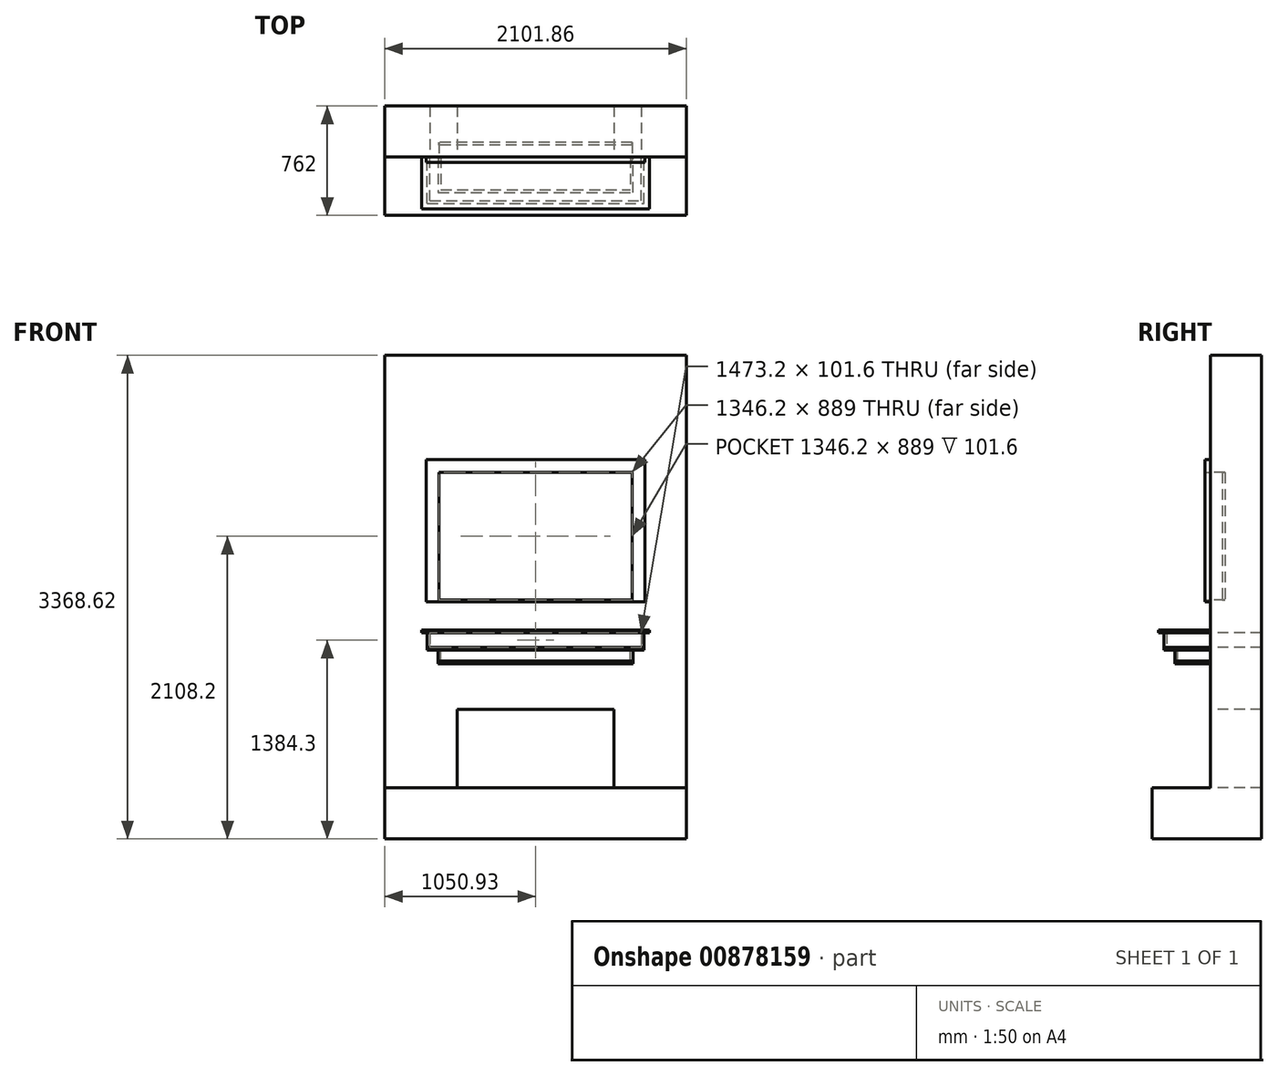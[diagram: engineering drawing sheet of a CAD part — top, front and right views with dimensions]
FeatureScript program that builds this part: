
annotation { "Feature Type Name" : "Feature", "Feature Type Description" : "" }
export const myFeature = defineFeature(function(context is Context, id is Id, definition is map)
    precondition{}
    {
        {
            var Q0;
            Q0=qCreatedBy(makeId("Front.planeOp"),FACE);
            var sketch = newSketch(context, id + "F0", { "sketchPlane" : qUnion([Q0])});
            skLineSegment(sketch, "E0.bottom", {"start": v(-736.6, 0) * mm, "end": v(736.6, 0) * mm});
            skLineSegment(sketch, "E0.top", {"start": v(-736.6, -101.6) * mm, "end": v(736.6, -101.6) * mm});
            skLineSegment(sketch, "E0.left", {"start": v(-736.6, 0) * mm, "end": v(-736.6, -101.6) * mm});
            skLineSegment(sketch, "E0.right", {"start": v(736.6, 0) * mm, "end": v(736.6, -101.6) * mm});
            skSolve(sketch);
        }
        {
            var Q0;
            Q0=makeQuery(id+"F0.imprint","IMPRINT",FACE,{"disambiguationData":[TD([[makeQuery(id+"F0.imprint","IMPRINT",EDGE,{"derivedFrom":sQuery(id+"F0.wireOp",EDGE,"E0.bottom")}),-1.0]])]});
            extrude(context, id + "F1", {"entities" : qUnion([Q0]), "depth" : 304.8 * mm, "offsetDistance" : 25.4 * mm});
        }
        {
            var Q0;
            Q0=makeQuery(id+"F1.opExtrude","SWEPT_FACE",FACE,{"disambiguationData":[OSD([sQuery(id+"F0.wireOp",EDGE,"E0.top")])]});
            var sketch = newSketch(context, id + "F2", { "sketchPlane" : qUnion([Q0])});
            skLineSegment(sketch, "E1.bottom", {"start": v(-755.65, 323.85) * mm, "end": v(755.65, 323.85) * mm});
            skLineSegment(sketch, "E1.top", {"start": v(-755.65, 304.8) * mm, "end": v(755.65, 304.8) * mm});
            skLineSegment(sketch, "E1.left", {"start": v(-755.65, 323.85) * mm, "end": v(-755.65, 304.8) * mm});
            skLineSegment(sketch, "E1.right", {"start": v(755.65, 323.85) * mm, "end": v(755.65, 304.8) * mm});
            skLineSegment(sketch, "E2.bottom", {"start": v(-755.65, 304.8) * mm, "end": v(-736.6, 304.8) * mm});
            skLineSegment(sketch, "E2.top", {"start": v(-755.65, 0) * mm, "end": v(-736.6, 0) * mm});
            skLineSegment(sketch, "E2.left", {"start": v(-755.65, 304.8) * mm, "end": v(-755.65, 0) * mm});
            skLineSegment(sketch, "E2.right", {"start": v(-736.6, 304.8) * mm, "end": v(-736.6, 0) * mm});
            skLineSegment(sketch, "E3.bottom", {"start": v(755.65, 304.8) * mm, "end": v(736.6, 304.8) * mm});
            skLineSegment(sketch, "E3.top", {"start": v(755.65, 0) * mm, "end": v(736.6, 0) * mm});
            skLineSegment(sketch, "E3.left", {"start": v(755.65, 304.8) * mm, "end": v(755.65, 0) * mm});
            skLineSegment(sketch, "E3.right", {"start": v(736.6, 304.8) * mm, "end": v(736.6, 0) * mm});
            skSolve(sketch);
        }
        {
            var Q0;
            Q0=makeQuery(id+"F2.imprint","IMPRINT",FACE,{"disambiguationData":[TD([[makeQuery(id+"F2.imprint","IMPRINT",EDGE,{"derivedFrom":sQuery(id+"F2.wireOp",EDGE,"E1.bottom")}),-1.0]])]});
            var Q1;
            Q1=makeQuery(id+"F2.imprint","IMPRINT",FACE,{"disambiguationData":[TD([[makeQuery(id+"F2.imprint","IMPRINT",EDGE,{"derivedFrom":sQuery(id+"F2.wireOp",EDGE,"E2.top")}),1.0]])]});
            var Q2;
            Q2=makeQuery(id+"F2.imprint","IMPRINT",FACE,{"disambiguationData":[TD([[makeQuery(id+"F2.imprint","IMPRINT",EDGE,{"derivedFrom":sQuery(id+"F2.wireOp",EDGE,"E3.top")}),-1.0]])]});
            var Q3;
            Q3=makeQuery(id+"F1.opExtrude","SWEPT_FACE",FACE,{"disambiguationData":[OSD([sQuery(id+"F0.wireOp",EDGE,"E0.bottom")])]});
            extrude(context, id + "F3", {"entities" : qUnion([Q0, Q1, Q2]), "endBound" : BoundingType.UP_TO_SURFACE, "oppositeDirection" : true, "depth" : 256.2 * mm, "endBoundEntityFace" : qUnion([Q3]), "offsetDistance" : 25.4 * mm});
        }
        {
            var Q0;
            Q0=makeQuery(id+"F1.opExtrude","SWEPT_FACE",FACE,{"disambiguationData":[OSD([sQuery(id+"F0.wireOp",EDGE,"E0.top")])]});
            var sketch = newSketch(context, id + "F4", { "sketchPlane" : qUnion([Q0])});
            skLineSegment(sketch, "E4.bottom", {"start": v(-755.65, 323.85) * mm, "end": v(755.65, 323.85) * mm});
            skLineSegment(sketch, "E4.top", {"start": v(-755.65, 0) * mm, "end": v(755.65, 0) * mm});
            skLineSegment(sketch, "E4.left", {"start": v(-755.65, 323.85) * mm, "end": v(-755.65, 0) * mm});
            skLineSegment(sketch, "E4.right", {"start": v(755.65, 323.85) * mm, "end": v(755.65, 0) * mm});
            skSolve(sketch);
        }
        {
            var Q0;
            Q0=makeQuery(id+"F4.imprint","IMPRINT",FACE,{"disambiguationData":[TD([[makeQuery(id+"F4.imprint","IMPRINT",EDGE,{"derivedFrom":sQuery(id+"F4.wireOp",EDGE,"E4.bottom")}),-1.0]])]});
            var Q1;
            {var subQ1=sQuery(id+"F0.wireOp",EDGE,"E0.top");Q1=makeQuery(id+"F4.imprint","IMPRINT",FACE,{"disambiguationData":[TD([[makeQuery(id+"F4.imprint","IMPRINT",EDGE,{"derivedFrom":makeQuery(id+"F1.opExtrude","CAP_EDGE",EDGE,{"disambiguationData":[OSD([subQ1])],"isStart":false})}),-1.0]])]});}
            extrude(context, id + "F5", {"entities" : qUnion([Q0, Q1]), "depth" : 19.05 * mm, "offsetDistance" : 25.4 * mm});
        }
        {
            var Q0;
            Q0=makeQuery(id+"F1.opExtrude","SWEPT_FACE",FACE,{"disambiguationData":[OSD([sQuery(id+"F0.wireOp",EDGE,"E0.bottom")])]});
            var sketch = newSketch(context, id + "F6", { "sketchPlane" : qUnion([Q0])});
            skLineSegment(sketch, "E5.bottom", {"start": v(-755.65, 0) * mm, "end": v(755.65, 0) * mm});
            skLineSegment(sketch, "E6", {"start": v(755.65, 0) * mm, "end": v(793.75, 0) * mm});
            skLineSegment(sketch, "E7", {"start": v(793.75, 0) * mm, "end": v(793.75, -361.95) * mm});
            skLineSegment(sketch, "E8", {"start": v(793.75, -361.95) * mm, "end": v(-793.75, -361.95) * mm});
            skLineSegment(sketch, "E9", {"start": v(-793.75, -361.95) * mm, "end": v(-793.75, 0) * mm});
            skLineSegment(sketch, "E10", {"start": v(-793.75, 0) * mm, "end": v(-755.65, 0) * mm});
            skLineSegment(sketch, "E11", {"start": v(755.65, -361.95) * mm, "end": v(755.65, -323.85) * mm, "construction": true});
            skSolve(sketch);
        }
        {
            var Q0;
            {var subQ1=sQuery(id+"F0.wireOp",EDGE,"E0.bottom");Q0=makeQuery(id+"F6.imprint","IMPRINT",FACE,{"disambiguationData":[TD([[makeQuery(id+"F6.imprint","IMPRINT",EDGE,{"derivedFrom":makeQuery(id+"F1.opExtrude","CAP_EDGE",EDGE,{"disambiguationData":[OSD([subQ1])],"isStart":false})}),1.0]])]});}
            var Q1;
            {var subQ0=sQuery(id+"F6.wireOp",EDGE,"E6");Q1=makeQuery(id+"F6.imprint","IMPRINT",FACE,{"disambiguationData":[TD([[makeQuery(id+"F6.imprint","IMPRINT",EDGE,{"derivedFrom":subQ0}),-1.0]])]});}
            extrude(context, id + "F7", {"entities" : qUnion([Q0, Q1]), "depth" : 19.05 * mm, "offsetDistance" : 25.4 * mm});
        }
        {
            var Q0;
            Q0=makeQuery(id+"F5.opExtrude","CAP_FACE",FACE,{"disambiguationData":[OSD([sQuery(id+"F4.wireOp",EDGE,"E4.bottom"),sQuery(id+"F4.wireOp",EDGE,"E4.top"),sQuery(id+"F4.wireOp",EDGE,"E4.left"),sQuery(id+"F4.wireOp",EDGE,"E4.right")])],"isStart":false});
            var sketch = newSketch(context, id + "F8", { "sketchPlane" : qUnion([Q0])});
            skLineSegment(sketch, "E12.bottom", {"start": v(-679.45, 0) * mm, "end": v(-660.4, 0) * mm});
            skLineSegment(sketch, "E12.top", {"start": v(-679.45, 228.6) * mm, "end": v(-660.4, 228.6) * mm});
            skLineSegment(sketch, "E12.left", {"start": v(-679.45, 0) * mm, "end": v(-679.45, 228.6) * mm});
            skLineSegment(sketch, "E12.right", {"start": v(-660.4, 0) * mm, "end": v(-660.4, 228.6) * mm});
            skLineSegment(sketch, "E13.bottom", {"start": v(679.45, 0) * mm, "end": v(660.4, 0) * mm});
            skLineSegment(sketch, "E13.top", {"start": v(679.45, 228.6) * mm, "end": v(660.4, 228.6) * mm});
            skLineSegment(sketch, "E13.left", {"start": v(679.45, 0) * mm, "end": v(679.45, 228.6) * mm});
            skLineSegment(sketch, "E13.right", {"start": v(660.4, 0) * mm, "end": v(660.4, 228.6) * mm});
            skLineSegment(sketch, "E14.bottom", {"start": v(-679.45, 247.65) * mm, "end": v(679.45, 247.65) * mm});
            skLineSegment(sketch, "E14.top", {"start": v(-679.45, 228.6) * mm, "end": v(679.45, 228.6) * mm});
            skLineSegment(sketch, "E14.left", {"start": v(-679.45, 247.65) * mm, "end": v(-679.45, 228.6) * mm});
            skLineSegment(sketch, "E14.right", {"start": v(679.45, 247.65) * mm, "end": v(679.45, 228.6) * mm});
            skLineSegment(sketch, "E15", {"start": v(-679.45, 247.65) * mm, "end": v(-755.65, 247.65) * mm, "construction": true});
            skLineSegment(sketch, "E16", {"start": v(679.45, 247.65) * mm, "end": v(755.65, 247.65) * mm, "construction": true});
            skLineSegment(sketch, "E17", {"start": v(-679.45, 247.65) * mm, "end": v(-679.45, 323.85) * mm, "construction": true});
            skSolve(sketch);
        }
        {
            var Q0;
            Q0=makeQuery(id+"F8.imprint","IMPRINT",FACE,{"disambiguationData":[TD([[makeQuery(id+"F8.imprint","IMPRINT",EDGE,{"derivedFrom":sQuery(id+"F8.wireOp",EDGE,"E12.bottom")}),1.0]])]});
            var Q1;
            Q1=makeQuery(id+"F8.imprint","IMPRINT",FACE,{"disambiguationData":[TD([[makeQuery(id+"F8.imprint","IMPRINT",EDGE,{"derivedFrom":sQuery(id+"F8.wireOp",EDGE,"E12.top")}),1.0]])]});
            var Q2;
            Q2=makeQuery(id+"F8.imprint","IMPRINT",FACE,{"disambiguationData":[TD([[makeQuery(id+"F8.imprint","IMPRINT",EDGE,{"derivedFrom":sQuery(id+"F8.wireOp",EDGE,"E13.bottom")}),1.0]])]});
            extrude(context, id + "F9", {"entities" : qUnion([Q0, Q1, Q2]), "depth" : 76.2 * mm, "offsetDistance" : 25.4 * mm});
        }
        {
            var Q0;
            Q0=makeQuery(id+"F9.opExtrude","CAP_FACE",FACE,{"disambiguationData":[OSD([sQuery(id+"F8.wireOp",EDGE,"E12.bottom"),sQuery(id+"F8.wireOp",EDGE,"E12.left"),sQuery(id+"F8.wireOp",EDGE,"E12.right"),sQuery(id+"F8.wireOp",EDGE,"E13.bottom"),sQuery(id+"F8.wireOp",EDGE,"E13.left"),sQuery(id+"F8.wireOp",EDGE,"E13.right"),sQuery(id+"F8.wireOp",EDGE,"E14.bottom"),sQuery(id+"F8.wireOp",EDGE,"E14.top"),sQuery(id+"F8.wireOp",EDGE,"E14.left"),sQuery(id+"F8.wireOp",EDGE,"E14.right")])],"isStart":false});
            var sketch = newSketch(context, id + "F10", { "sketchPlane" : qUnion([Q0])});
            skLineSegment(sketch, "E18.bottom", {"start": v(679.45, 247.65) * mm, "end": v(-679.45, 247.65) * mm});
            skLineSegment(sketch, "E18.top", {"start": v(679.45, 0) * mm, "end": v(-679.45, 0) * mm});
            skLineSegment(sketch, "E18.left", {"start": v(679.45, 247.65) * mm, "end": v(679.45, 0) * mm});
            skLineSegment(sketch, "E18.right", {"start": v(-679.45, 247.65) * mm, "end": v(-679.45, 0) * mm});
            skSolve(sketch);
        }
        {
            var Q0;
            Q0=makeQuery(id+"F10.imprint","IMPRINT",FACE,{"disambiguationData":[TD([[makeQuery(id+"F10.imprint","IMPRINT",EDGE,{"derivedFrom":sQuery(id+"F10.wireOp",EDGE,"E18.bottom")}),-1.0]])]});
            var Q1;
            {var subQ1=makeQuery(id+"F9.opExtrude","CAP_EDGE",EDGE,{"disambiguationData":[OSD([sQuery(id+"F8.wireOp",EDGE,"E12.right")])],"isStart":false});Q1=makeQuery(id+"F10.imprint","IMPRINT",FACE,{"disambiguationData":[TD([[makeQuery(id+"F10.imprint","IMPRINT",EDGE,{"derivedFrom":subQ1}),-1.0]])]});}
            extrude(context, id + "F11", {"entities" : qUnion([Q0, Q1]), "depth" : 19.05 * mm, "offsetDistance" : 25.4 * mm});
        }
        {
            var Q0;
            Q0=makeQuery(id+"F1.opExtrude","CAP_FACE",FACE,{"disambiguationData":[OSD([sQuery(id+"F0.wireOp",EDGE,"E0.bottom"),sQuery(id+"F0.wireOp",EDGE,"E0.top"),sQuery(id+"F0.wireOp",EDGE,"E0.left"),sQuery(id+"F0.wireOp",EDGE,"E0.right")])],"isStart":true});
            var sketch = newSketch(context, id + "F12", { "sketchPlane" : qUnion([Q0])});
            skLineSegment(sketch, "E19.top", {"start": v(-1050.93, -1079.5) * mm, "end": v(1050.93, -1079.5) * mm});
            skLineSegment(sketch, "E19.left", {"start": v(-1050.93, 1117.6) * mm, "end": v(-1050.93, -1079.5) * mm});
            skLineSegment(sketch, "E19.right", {"start": v(1050.93, 1117.6) * mm, "end": v(1050.93, -1079.5) * mm});
            skLineSegment(sketch, "E20", {"start": v(0, 1117.6) * mm, "end": v(0, -1079.5) * mm, "construction": true});
            skPoint(sketch, "E21", {"position": v(0, 19.05) * mm});
            skLineSegment(sketch, "E22.bottom", {"start": v(-673.1, 1117.6) * mm, "end": v(673.1, 1117.6) * mm});
            skLineSegment(sketch, "E22.top", {"start": v(-673.1, 228.6) * mm, "end": v(673.1, 228.6) * mm});
            skLineSegment(sketch, "E22.left", {"start": v(-673.1, 1117.6) * mm, "end": v(-673.1, 228.6) * mm});
            skLineSegment(sketch, "E22.right", {"start": v(673.1, 1117.6) * mm, "end": v(673.1, 228.6) * mm});
            skPoint(sketch, "E23", {"position": v(0, 1117.6) * mm});
            skLineSegment(sketch, "E24.bottom", {"start": v(-546.1, -1079.5) * mm, "end": v(546.1, -1079.5) * mm});
            skLineSegment(sketch, "E24.top", {"start": v(-546.1, -533.4) * mm, "end": v(546.1, -533.4) * mm});
            skLineSegment(sketch, "E24.left", {"start": v(-546.1, -1079.5) * mm, "end": v(-546.1, -533.4) * mm});
            skLineSegment(sketch, "E24.right", {"start": v(546.1, -1079.5) * mm, "end": v(546.1, -533.4) * mm});
            skPoint(sketch, "E25", {"position": v(0, -533.4) * mm});
            skLineSegment(sketch, "E26.top", {"start": v(1050.93, 1933.52) * mm, "end": v(-1050.92, 1933.52) * mm});
            skLineSegment(sketch, "E26.left", {"start": v(1050.93, 1117.6) * mm, "end": v(1050.93, 1933.52) * mm});
            skLineSegment(sketch, "E26.right", {"start": v(-1050.92, 1117.6) * mm, "end": v(-1050.92, 1933.52) * mm});
            skLineSegment(sketch, "E27", {"start": v(0, 1117.6) * mm, "end": v(0, 1933.52) * mm, "construction": true});
            skSolve(sketch);
        }
        {
            var Q0;
            {var subQ4=sQuery(id+"F12.wireOp",EDGE,"E19.left");Q0=makeQuery(id+"F12.imprint","IMPRINT",FACE,{"disambiguationData":[TD([[makeQuery(id+"F12.imprint","IMPRINT",EDGE,{"derivedFrom":subQ4}),1.0]])]});}
            var Q1;
            Q1=makeQuery(id+"F12.imprint","IMPRINT",FACE,{"disambiguationData":[TD([[makeQuery(id+"F12.imprint","IMPRINT",EDGE,{"derivedFrom":sQuery(id+"F12.wireOp",EDGE,"E22.bottom")}),-1.0]])]});
            extrude(context, id + "F13", {"entities" : qUnion([Q0, Q1]), "depth" : 355.6 * mm, "offsetDistance" : 25.4 * mm});
        }
        {
            var Q0;
            Q0=makeQuery(id+"F12.imprint","IMPRINT",FACE,{"disambiguationData":[TD([[makeQuery(id+"F12.imprint","IMPRINT",EDGE,{"derivedFrom":sQuery(id+"F12.wireOp",EDGE,"E22.bottom")}),-1.0]])]});
            extrude(context, id + "F14", {"entities" : qUnion([Q0]), "operationType" : NewBodyOperationType.REMOVE, "depth" : 101.6 * mm, "offsetDistance" : 25.4 * mm});
        }
        {
            var Q0;
            {var subQ0=sQuery(id+"F12.wireOp",EDGE,"E19.top");Q0=makeQuery(id+"F13.opExtrude","SWEPT_FACE",FACE,{"disambiguationData":[OSD([subQ0]),TDD([makeQuery(id+"F12.imprint","IMPRINT",EDGE,{"disambiguationData":[TD([[makeQuery(id+"F12.imprint","INTERSECT",VERTEX,{"derivedFrom":[subQ0,sQuery(id+"F12.wireOp",EDGE,"E19.right")]}),1.0]])],"derivedFrom":subQ0})])]});}
            var sketch = newSketch(context, id + "F15", { "sketchPlane" : qUnion([Q0])});
            skLineSegment(sketch, "E28.bottom", {"start": v(-1050.93, -355.6) * mm, "end": v(1050.92, -355.6) * mm});
            skLineSegment(sketch, "E28.top", {"start": v(-1050.93, 406.4) * mm, "end": v(1050.92, 406.4) * mm});
            skLineSegment(sketch, "E28.left", {"start": v(-1050.93, -355.6) * mm, "end": v(-1050.93, 406.4) * mm});
            skLineSegment(sketch, "E28.right", {"start": v(1050.93, -355.6) * mm, "end": v(1050.93, 406.4) * mm});
            skSolve(sketch);
        }
        {
            var Q0;
            {var subQ5=sQuery(id+"F15.wireOp",EDGE,"E28.top");Q0=makeQuery(id+"F15.imprint","IMPRINT",FACE,{"disambiguationData":[TD([[makeQuery(id+"F15.imprint","IMPRINT",EDGE,{"derivedFrom":subQ5}),-1.0]])]});}
            var Q1;
            {var subQ3=sQuery(id+"F12.wireOp",EDGE,"E24.right");var subQ4=sQuery(id+"F12.wireOp",EDGE,"E19.top");var subQ5=makeQuery(id+"F13.opExtrude","SWEPT_EDGE",EDGE,{"disambiguationData":[OSD([subQ4,subQ3])]});Q1=makeQuery(id+"F15.imprint","IMPRINT",FACE,{"disambiguationData":[TD([[makeQuery(id+"F15.imprint","IMPRINT",EDGE,{"derivedFrom":subQ5}),1.0]])]});}
            extrude(context, id + "F16", {"entities" : qUnion([Q0, Q1]), "operationType" : NewBodyOperationType.ADD, "depth" : 355.6 * mm, "offsetDistance" : 25.4 * mm});
        }
        {
            var Q0;
            Q0=makeQuery(id+"F13.opExtrude","CAP_FACE",FACE,{"disambiguationData":[OSD([sQuery(id+"F0.wireOp",EDGE,"E0.bottom"),sQuery(id+"F0.wireOp",EDGE,"E0.top"),sQuery(id+"F0.wireOp",EDGE,"E0.left"),sQuery(id+"F0.wireOp",EDGE,"E0.right"),sQuery(id+"F12.wireOp",EDGE,"E19.top"),sQuery(id+"F12.wireOp",EDGE,"E19.left"),sQuery(id+"F12.wireOp",EDGE,"E19.right"),sQuery(id+"F12.wireOp",EDGE,"E24.top"),sQuery(id+"F12.wireOp",EDGE,"E24.left"),sQuery(id+"F12.wireOp",EDGE,"E24.right"),sQuery(id+"F12.wireOp",EDGE,"E26.top"),sQuery(id+"F12.wireOp",EDGE,"E26.left"),sQuery(id+"F12.wireOp",EDGE,"E26.right")])],"isStart":true});
            var sketch = newSketch(context, id + "F17", { "sketchPlane" : qUnion([Q0])});
            skLineSegment(sketch, "E29.bottom", {"start": v(-552.45, -215.9) * mm, "end": v(-400.05, -215.9) * mm});
            skLineSegment(sketch, "E29.top", {"start": v(-552.45, -444.5) * mm, "end": v(-400.05, -444.5) * mm, "construction": true});
            skLineSegment(sketch, "E29.left", {"start": v(-552.45, -215.9) * mm, "end": v(-552.45, -444.5) * mm});
            skLineSegment(sketch, "E29.right", {"start": v(-400.05, -215.9) * mm, "end": v(-400.05, -444.5) * mm});
            skLineSegment(sketch, "E30.bottom", {"start": v(400.05, -215.9) * mm, "end": v(552.45, -215.9) * mm});
            skLineSegment(sketch, "E30.top", {"start": v(400.05, -444.5) * mm, "end": v(552.45, -444.5) * mm, "construction": true});
            skLineSegment(sketch, "E30.left", {"start": v(400.05, -215.9) * mm, "end": v(400.05, -444.5) * mm});
            skLineSegment(sketch, "E30.right", {"start": v(552.45, -215.9) * mm, "end": v(552.45, -444.5) * mm});
            skLineSegment(sketch, "E31", {"start": v(-552.45, -215.9) * mm, "end": v(-679.45, -215.9) * mm, "construction": true});
            skLineSegment(sketch, "E32", {"start": v(552.45, -215.9) * mm, "end": v(679.45, -215.9) * mm, "construction": true});
            skLineSegment(sketch, "E33", {"start": v(-476.25, -444.5) * mm, "end": v(-476.25, -215.9) * mm});
            skLineSegment(sketch, "E34", {"start": v(476.25, -444.5) * mm, "end": v(476.25, -215.9) * mm});
            skLineSegment(sketch, "E35", {"start": v(-552.45, -215.9) * mm, "end": v(-514.35, -444.5) * mm});
            skLineSegment(sketch, "E36", {"start": v(-438.15, -444.5) * mm, "end": v(-400.05, -215.9) * mm});
            skLineSegment(sketch, "E37", {"start": v(400.05, -215.9) * mm, "end": v(438.15, -444.5) * mm});
            skLineSegment(sketch, "E38", {"start": v(514.35, -444.5) * mm, "end": v(552.45, -215.9) * mm});
            skLineSegment(sketch, "E39", {"start": v(-514.35, -444.5) * mm, "end": v(-438.15, -444.5) * mm});
            skLineSegment(sketch, "E40", {"start": v(438.15, -444.5) * mm, "end": v(514.35, -444.5) * mm});
            skSolve(sketch);
        }
        {
            var Q0;
            {var subQ2=sQuery(id+"F17.wireOp",EDGE,"E34");Q0=makeQuery(id+"F17.imprint","IMPRINT",FACE,{"disambiguationData":[TD([[makeQuery(id+"F17.imprint","IMPRINT",EDGE,{"derivedFrom":subQ2}),1.0]])]});}
            var Q1;
            {var subQ2=sQuery(id+"F17.wireOp",EDGE,"E33");Q1=makeQuery(id+"F17.imprint","IMPRINT",FACE,{"disambiguationData":[TD([[makeQuery(id+"F17.imprint","IMPRINT",EDGE,{"derivedFrom":subQ2}),-1.0]])]});}
            var Q2;
            {var subQ2=sQuery(id+"F17.wireOp",EDGE,"E34");Q2=makeQuery(id+"F17.imprint","IMPRINT",FACE,{"disambiguationData":[TD([[makeQuery(id+"F17.imprint","IMPRINT",EDGE,{"derivedFrom":subQ2}),-1.0]])]});}
            var Q3;
            {var subQ2=sQuery(id+"F17.wireOp",EDGE,"E33");Q3=makeQuery(id+"F17.imprint","IMPRINT",FACE,{"disambiguationData":[TD([[makeQuery(id+"F17.imprint","IMPRINT",EDGE,{"derivedFrom":subQ2}),1.0]])]});}
            extrude(context, id + "F18", {"entities" : qUnion([Q0, Q1, Q2, Q3]), "depth" : 127 * mm, "offsetDistance" : 25.4 * mm});
        }
        {
            var Q0;
            Q0=makeQuery(id+"F9.opExtrude","SWEPT_FACE",FACE,{"disambiguationData":[OSD([sQuery(id+"F8.wireOp",EDGE,"E12.left"),sQuery(id+"F8.wireOp",EDGE,"E14.left")])]});
            var sketch = newSketch(context, id + "F19", { "sketchPlane" : qUnion([Q0])});
            skLineSegment(sketch, "E41", {"start": v(127, -215.9) * mm, "end": v(50.8, -444.5) * mm});
            skLineSegment(sketch, "E42", {"start": v(50.8, -444.5) * mm, "end": v(127, -444.5) * mm});
            skLineSegment(sketch, "E43", {"start": v(127, -444.5) * mm, "end": v(127, -215.9) * mm});
            skSolve(sketch);
        }
        {
            var Q0;
            Q0=makeQuery(id+"F19.imprint","IMPRINT",FACE,{"disambiguationData":[TD([[makeQuery(id+"F19.imprint","IMPRINT",EDGE,{"derivedFrom":sQuery(id+"F19.wireOp",EDGE,"E41")}),1.0]])]});
            extrude(context, id + "F20", {"entities" : qUnion([Q0]), "operationType" : NewBodyOperationType.REMOVE, "oppositeDirection" : true, "depth" : 1468.66 * mm, "offsetDistance" : 25.4 * mm});
        }
        {
            var Q0;
            Q0=makeQuery(id+"F13.opExtrude","CAP_FACE",FACE,{"disambiguationData":[OSD([sQuery(id+"F0.wireOp",EDGE,"E0.bottom"),sQuery(id+"F0.wireOp",EDGE,"E0.top"),sQuery(id+"F0.wireOp",EDGE,"E0.left"),sQuery(id+"F0.wireOp",EDGE,"E0.right"),sQuery(id+"F12.wireOp",EDGE,"E19.top"),sQuery(id+"F12.wireOp",EDGE,"E19.left"),sQuery(id+"F12.wireOp",EDGE,"E19.right"),sQuery(id+"F12.wireOp",EDGE,"E24.top"),sQuery(id+"F12.wireOp",EDGE,"E24.left"),sQuery(id+"F12.wireOp",EDGE,"E24.right"),sQuery(id+"F12.wireOp",EDGE,"E26.top"),sQuery(id+"F12.wireOp",EDGE,"E26.left"),sQuery(id+"F12.wireOp",EDGE,"E26.right")])],"isStart":true});
            var sketch = newSketch(context, id + "F21", { "sketchPlane" : qUnion([Q0])});
            skLineSegment(sketch, "E44.bottom", {"start": v(-762, 1206.5) * mm, "end": v(762, 1206.5) * mm});
            skLineSegment(sketch, "E44.top", {"start": v(-673.1, 304.8) * mm, "end": v(673.1, 304.8) * mm});
            skLineSegment(sketch, "E44.right", {"start": v(762, 1206.5) * mm, "end": v(762, 1117.6) * mm});
            skLineSegment(sketch, "E45.bottom", {"start": v(-673.1, 1117.6) * mm, "end": v(673.1, 1117.6) * mm});
            skLineSegment(sketch, "E45.top", {"start": v(-673.1, 228.6) * mm, "end": v(673.1, 228.6) * mm});
            skLineSegment(sketch, "E45.left", {"start": v(-673.1, 1117.6) * mm, "end": v(-673.1, 228.6) * mm});
            skLineSegment(sketch, "E45.right", {"start": v(673.1, 1117.6) * mm, "end": v(673.1, 228.6) * mm});
            skLineSegment(sketch, "E46", {"start": v(673.1, 1117.6) * mm, "end": v(762, 1117.6) * mm, "construction": true});
            skLineSegment(sketch, "E47", {"start": v(-673.1, 1117.6) * mm, "end": v(-762, 1117.6) * mm, "construction": true});
            skLineSegment(sketch, "E48", {"start": v(-673.1, 1117.6) * mm, "end": v(-673.1, 1206.5) * mm, "construction": true});
            skLineSegment(sketch, "E49", {"start": v(0, 304.8) * mm, "end": v(0, 228.6) * mm, "construction": true});
            skLineSegment(sketch, "E50.top", {"start": v(-762, 215.9) * mm, "end": v(762, 215.9) * mm});
            skLineSegment(sketch, "E51", {"start": v(-762, 1206.5) * mm, "end": v(-762, 215.9) * mm});
            skLineSegment(sketch, "E52", {"start": v(762, 215.9) * mm, "end": v(762, 1117.6) * mm});
            skLineSegment(sketch, "E53", {"start": v(-673.1, 215.9) * mm, "end": v(-673.1, 304.8) * mm, "construction": true});
            skSolve(sketch);
        }
        {
            var Q0;
            Q0=makeQuery(id+"F21.imprint","IMPRINT",FACE,{"disambiguationData":[TD([[makeQuery(id+"F21.imprint","IMPRINT",EDGE,{"derivedFrom":sQuery(id+"F21.wireOp",EDGE,"E44.bottom")}),-1.0]])]});
            extrude(context, id + "F22", {"entities" : qUnion([Q0]), "depth" : 38.1 * mm, "offsetDistance" : 25.4 * mm});
        }
        {
            var Q0;
            Q0=makeQuery(id+"F14.boolean.opBoolean","COPY",FACE,{"derivedFrom":makeQuery(id+"F14.opExtrude","CAP_FACE",FACE,{"disambiguationData":[OSD([sQuery(id+"F12.wireOp",EDGE,"E22.bottom"),sQuery(id+"F12.wireOp",EDGE,"E22.top"),sQuery(id+"F12.wireOp",EDGE,"E22.left"),sQuery(id+"F12.wireOp",EDGE,"E22.right")])],"isStart":false})});
            extrude(context, id + "F23", {"entities" : qUnion([Q0]), "depth" : 19.05 * mm, "offsetDistance" : 25.4 * mm});
        }
        {
            var Q0;
            Q0=makeQuery(id+"F18.opExtrude","SWEPT_BODY",BODY,{"disambiguationData":[OSD([sQuery(id+"F17.wireOp",EDGE,"E29.bottom"),sQuery(id+"F17.wireOp",EDGE,"E35"),sQuery(id+"F17.wireOp",EDGE,"E36"),sQuery(id+"F17.wireOp",EDGE,"E39")])]});
            deleteBodies(context, id + "F24", {"entities" : qUnion([Q0])});
        }
        {
            var Q0;
            Q0=makeQuery(id+"F18.opExtrude","SWEPT_BODY",BODY,{"disambiguationData":[OSD([sQuery(id+"F17.wireOp",EDGE,"E30.bottom"),sQuery(id+"F17.wireOp",EDGE,"E37"),sQuery(id+"F17.wireOp",EDGE,"E38"),sQuery(id+"F17.wireOp",EDGE,"E40")])]});
            deleteBodies(context, id + "F25", {"entities" : qUnion([Q0])});
        }
    });
